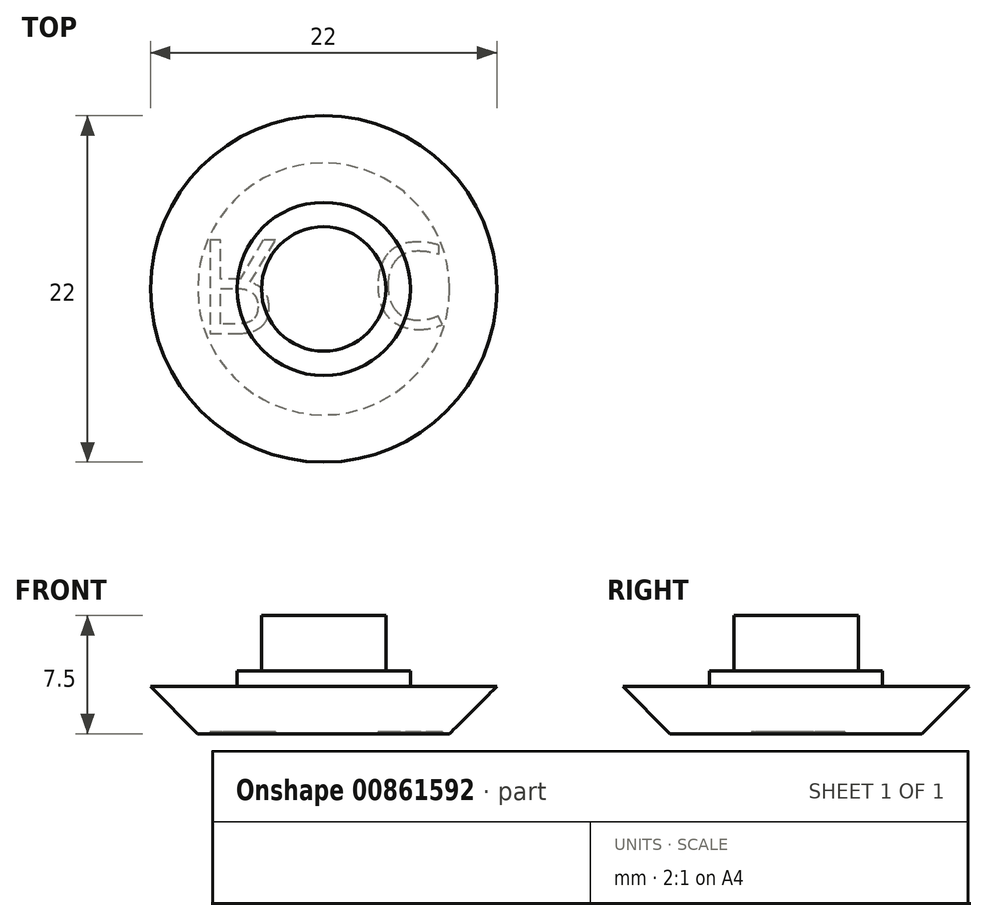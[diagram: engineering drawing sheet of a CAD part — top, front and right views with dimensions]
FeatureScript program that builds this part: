
annotation { "Feature Type Name" : "Feature", "Feature Type Description" : "" }
export const myFeature = defineFeature(function(context is Context, id is Id, definition is map)
    precondition{}
    {
        {
            var Q0;
            Q0=qCreatedBy(makeId("Front.planeOp"),FACE);
            var sketch = newSketch(context, id + "F0", { "sketchPlane" : qUnion([Q0])});
            skLineSegment(sketch, "E0", {"start": v(0, 7.5) * mm, "end": v(-3.95, 7.5) * mm});
            skLineSegment(sketch, "E1", {"start": v(-3.95, 7.5) * mm, "end": v(-3.95, 4) * mm});
            skLineSegment(sketch, "E2", {"start": v(-3.95, 4) * mm, "end": v(-5.5, 4) * mm});
            skLineSegment(sketch, "E3", {"start": v(-5.5, 4) * mm, "end": v(-5.5, 3) * mm});
            skLineSegment(sketch, "E4", {"start": v(-5.5, 3) * mm, "end": v(-11, 3) * mm});
            skLineSegment(sketch, "E5", {"start": v(-11, 3) * mm, "end": v(-11, 0) * mm});
            skLineSegment(sketch, "E6", {"start": v(-11, 0) * mm, "end": v(0, 0) * mm});
            skLineSegment(sketch, "E7", {"start": v(0, 0) * mm, "end": v(0, 7.5) * mm});
            skPoint(sketch, "E8.center.orphan", {"position": v(-420.56, -246.15) * mm});
            skPoint(sketch, "E8.end.orphan", {"position": v(-420.56, -275.96) * mm});
            skSolve(sketch);
        }
        {
            var Q0;
            Q0=makeQuery(id+"F0.imprint","IMPRINT",FACE,{"disambiguationData":[TD([[makeQuery(id+"F0.imprint","IMPRINT",EDGE,{"derivedFrom":sQuery(id+"F0.wireOp",EDGE,"E0")}),1.0]])]});
            var Q1;
            Q1=sQuery(id+"F0.wireOp",EDGE,"E7");
            revolve(context, id + "F1", {"surfaceOperationType" : NewSurfaceOperationType.NEW, "entities" : qUnion([Q0]), "axis" : qUnion([Q1]), "revolveType" : RevolveType.FULL});
        }
        {
            var Q0;
            Q0=makeQuery(id+"F1.opRevolve","SWEPT_EDGE",EDGE,{"disambiguationData":[OSD([sQuery(id+"F0.wireOp",EDGE,"E5"),sQuery(id+"F0.wireOp",EDGE,"E6")])]});
            chamfer(context, id + "F2", {"entities" : qUnion([Q0]), "width" : 3 * mm, "tangentPropagation" : true});
        }
        {
            var Q0;
            Q0=makeQuery(id+"F1.opRevolve","SWEPT_FACE",FACE,{"disambiguationData":[OSD([sQuery(id+"F0.wireOp",EDGE,"E6")])]});
            var sketch = newSketch(context, id + "F3", { "sketchPlane" : qUnion([Q0])});
            skText(sketch, "E9", { "text": "R", "fontName": "OpenSans-Regular.ttf"});
            const initialGuessF3  = {"E9": [-0.00805, -0.0031, 1, 0, 0.00599]};
            skSetInitialGuess(sketch, initialGuessF3);
            skSolve(sketch);
        }
        {
            var Q0;
            Q0=makeQuery(id+"F3.imprint","IMPRINT",FACE,{"disambiguationData":[TD([[makeQuery(id+"F3.imprint","IMPRINT",EDGE,{"derivedFrom":sQuery(id+"F3.wireOp",EDGE,"E9.sketch_text.stroke-0")}),1.0]])]});
            var sketch = newSketch(context, id + "F4", { "sketchPlane" : qUnion([Q0])});
            skText(sketch, "E10", { "text": "C", "fontName": "OpenSans-Regular.ttf"});
            const initialGuessF4  = {"E10": [0.00298, -0.00291, 1, 0, 0.00545]};
            skSetInitialGuess(sketch, initialGuessF4);
            skSolve(sketch);
        }
        {
            var Q0;
            Q0 = qSketchRegion(id + "F3", true);
            var Q1;
            Q1 = qSketchRegion(id + "F4", true);
            extrude(context, id + "F5", {"entities" : qUnion([Q0, Q1]), "operationType" : NewBodyOperationType.REMOVE, "oppositeDirection" : true, "depth" : 0.1 * mm, "offsetDistance" : 25 * mm});
        }
    });
